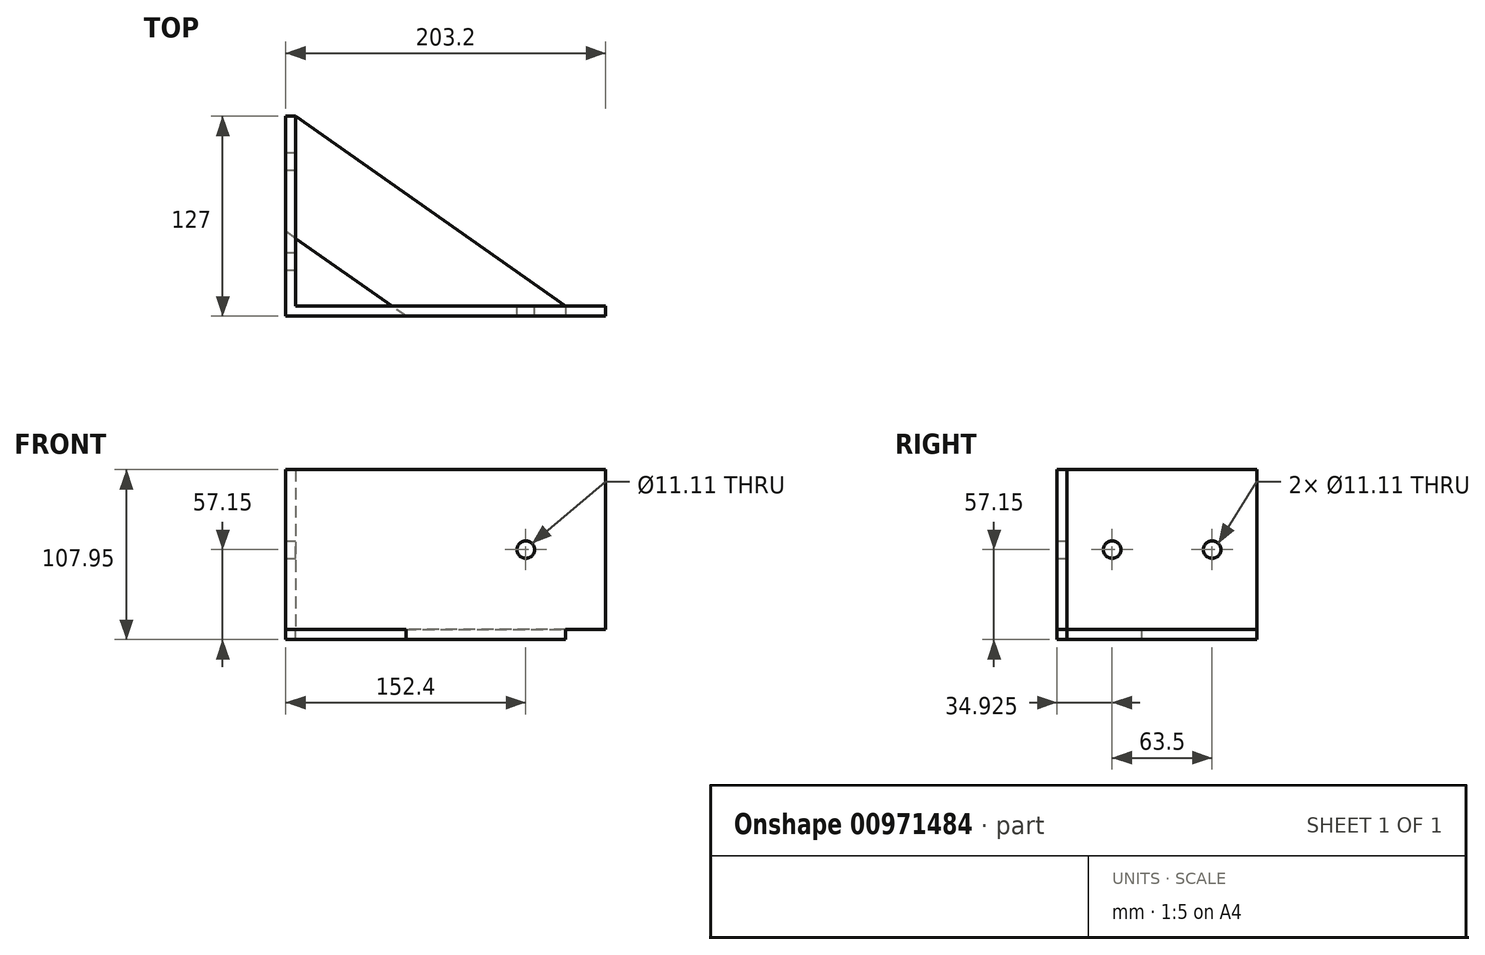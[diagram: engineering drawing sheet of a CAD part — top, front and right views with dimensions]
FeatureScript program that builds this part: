
annotation { "Feature Type Name" : "Feature", "Feature Type Description" : "" }
export const myFeature = defineFeature(function(context is Context, id is Id, definition is map)
    precondition{}
    {
        {
            var Q0;
            Q0=qCreatedBy(makeId("Top.planeOp"),FACE);
            var sketch = newSketch(context, id + "F0", { "sketchPlane" : qUnion([Q0])});
            skLineSegment(sketch, "E0", {"start": v(0, 127) * mm, "end": v(0, 0) * mm});
            skLineSegment(sketch, "E1", {"start": v(0, 0) * mm, "end": v(203.2, 0) * mm});
            skLineSegment(sketch, "E2", {"start": v(203.2, 0) * mm, "end": v(203.2, 6.35) * mm});
            skLineSegment(sketch, "E3", {"start": v(203.2, 6.35) * mm, "end": v(6.35, 6.35) * mm});
            skLineSegment(sketch, "E4", {"start": v(6.35, 6.35) * mm, "end": v(6.35, 127) * mm});
            skLineSegment(sketch, "E5", {"start": v(6.35, 127) * mm, "end": v(0, 127) * mm});
            skSolve(sketch);
        }
        {
            var Q0;
            Q0 = qSketchRegion(id + "F0", true);
            extrude(context, id + "F1", {"entities" : qUnion([Q0]), "depth" : 101.6 * mm, "offsetDistance" : 25.4 * mm});
        }
        {
            var Q0;
            Q0=makeQuery(id+"F1.opExtrude","CAP_FACE",FACE,{"disambiguationData":[OSD([sQuery(id+"F0.wireOp",EDGE,"E0"),sQuery(id+"F0.wireOp",EDGE,"E1"),sQuery(id+"F0.wireOp",EDGE,"E2"),sQuery(id+"F0.wireOp",EDGE,"E3"),sQuery(id+"F0.wireOp",EDGE,"E4"),sQuery(id+"F0.wireOp",EDGE,"E5")])],"isStart":true});
            var sketch = newSketch(context, id + "F2", { "sketchPlane" : qUnion([Q0])});
            skLineSegment(sketch, "E6", {"start": v(6.35, -127) * mm, "end": v(177.8, -6.35) * mm});
            skLineSegment(sketch, "E7", {"start": v(177.8, 0) * mm, "end": v(76.48, 0) * mm});
            skLineSegment(sketch, "E8", {"start": v(76.48, 0) * mm, "end": v(0, -53.82) * mm});
            skLineSegment(sketch, "E9", {"start": v(0, -53.82) * mm, "end": v(0, -127) * mm});
            skLineSegment(sketch, "E10", {"start": v(6.35, -127) * mm, "end": v(0, -127) * mm});
            skPoint(sketch, "E11.orphan", {"position": v(0, -131.47) * mm});
            skLineSegment(sketch, "E12", {"start": v(177.8, -6.35) * mm, "end": v(177.8, 0) * mm});
            skSolve(sketch);
        }
        {
            var Q0;
            Q0 = qSketchRegion(id + "F2", true);
            extrude(context, id + "F3", {"entities" : qUnion([Q0]), "operationType" : NewBodyOperationType.ADD, "depth" : 6.35 * mm, "offsetDistance" : 25.4 * mm});
        }
        {
            var Q0;
            Q0=makeQuery(id+"F1.opExtrude","SWEPT_FACE",FACE,{"disambiguationData":[OSD([sQuery(id+"F0.wireOp",EDGE,"E4")])]});
            var sketch = newSketch(context, id + "F4", { "sketchPlane" : qUnion([Q0])});
            skCircle(sketch, "E13", {"center": v(34.93, 50.8) * mm, "radius": 5.56 * mm});
            skCircle(sketch, "E14", {"center": v(98.43, 50.8) * mm, "radius": 5.56 * mm});
            skLineSegment(sketch, "E15", {"start": v(98.43, 50.8) * mm, "end": v(34.93, 50.8) * mm, "construction": true});
            skLineSegment(sketch, "E16", {"start": v(66.68, 50.8) * mm, "end": v(66.68, 101.6) * mm, "construction": true});
            skSolve(sketch);
        }
        {
            var Q0;
            Q0 = qSketchRegion(id + "F4", true);
            extrude(context, id + "F5", {"entities" : qUnion([Q0]), "operationType" : NewBodyOperationType.REMOVE, "endBound" : BoundingType.THROUGH_ALL, "oppositeDirection" : true, "depth" : 25.4 * mm, "offsetDistance" : 25.4 * mm});
        }
        {
            var Q0;
            Q0=makeQuery(id+"F1.opExtrude","SWEPT_FACE",FACE,{"disambiguationData":[OSD([sQuery(id+"F0.wireOp",EDGE,"E3")])]});
            var sketch = newSketch(context, id + "F6", { "sketchPlane" : qUnion([Q0])});
            skCircle(sketch, "E17", {"center": v(-152.4, 50.8) * mm, "radius": 5.56 * mm});
            skLineSegment(sketch, "E18", {"start": v(-203.2, 50.8) * mm, "end": v(-152.4, 50.8) * mm, "construction": true});
            skSolve(sketch);
        }
        {
            var Q0;
            Q0 = qSketchRegion(id + "F6", true);
            extrude(context, id + "F7", {"entities" : qUnion([Q0]), "operationType" : NewBodyOperationType.REMOVE, "endBound" : BoundingType.THROUGH_ALL, "oppositeDirection" : true, "depth" : 25.4 * mm, "offsetDistance" : 25.4 * mm});
        }
    });
